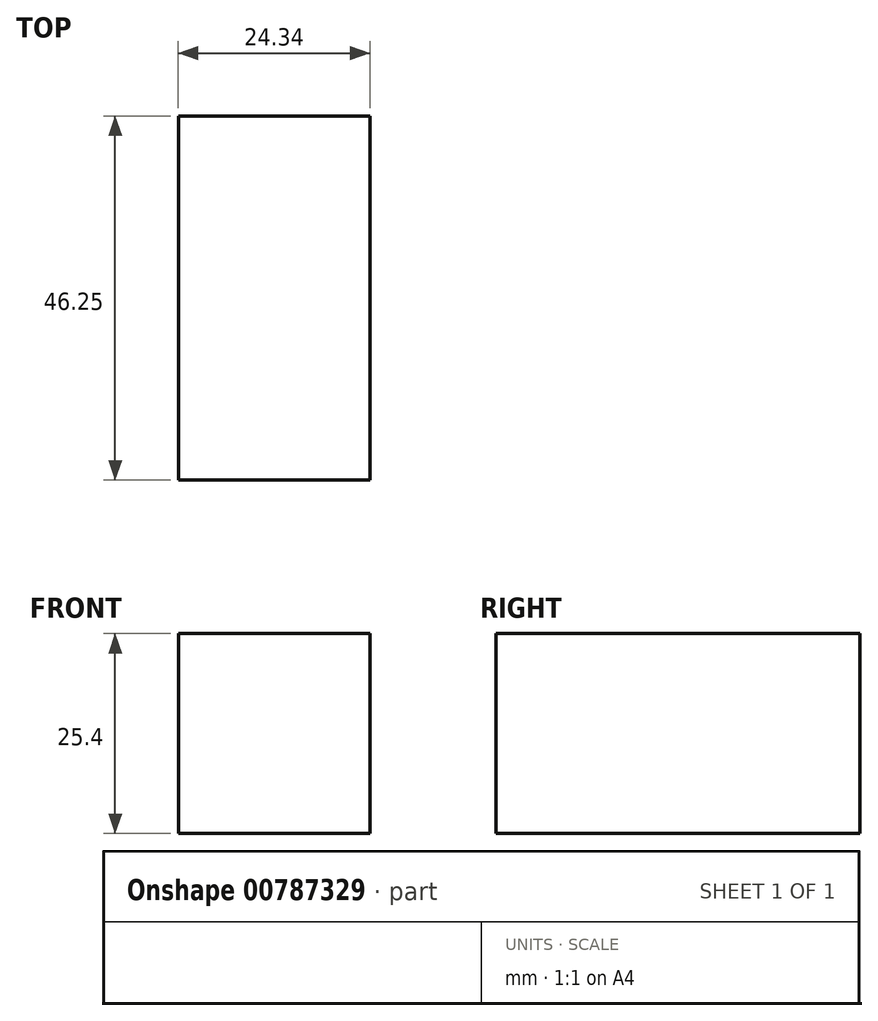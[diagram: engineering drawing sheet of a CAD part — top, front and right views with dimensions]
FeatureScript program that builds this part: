
annotation { "Feature Type Name" : "Feature", "Feature Type Description" : "" }
export const myFeature = defineFeature(function(context is Context, id is Id, definition is map)
    precondition{}
    {
        {
            var Q0;
            Q0=qCreatedBy(makeId("Top.planeOp"),FACE);
            var sketch = newSketch(context, id + "F0", { "sketchPlane" : qUnion([Q0])});
            skLineSegment(sketch, "E0.bottom", {"start": v(-0.05, 0.76) * mm, "end": v(24.3, 0.76) * mm});
            skLineSegment(sketch, "E0.top", {"start": v(-0.05, 47) * mm, "end": v(24.3, 47) * mm});
            skLineSegment(sketch, "E0.left", {"start": v(-0.05, 0.76) * mm, "end": v(-0.05, 47) * mm});
            skLineSegment(sketch, "E0.right", {"start": v(24.3, 0.76) * mm, "end": v(24.3, 47) * mm});
            skSolve(sketch);
        }
        {
            var Q0;
            Q0=makeQuery(id+"F0.imprint","IMPRINT",FACE,{"disambiguationData":[TD([[makeQuery(id+"F0.imprint","IMPRINT",EDGE,{"derivedFrom":sQuery(id+"F0.wireOp",EDGE,"E0.bottom")}),1.0]])]});
            extrude(context, id + "F1", {"entities" : qUnion([Q0]), "depth" : 25.4 * mm, "offsetDistance" : 25.4 * mm});
        }
    });
